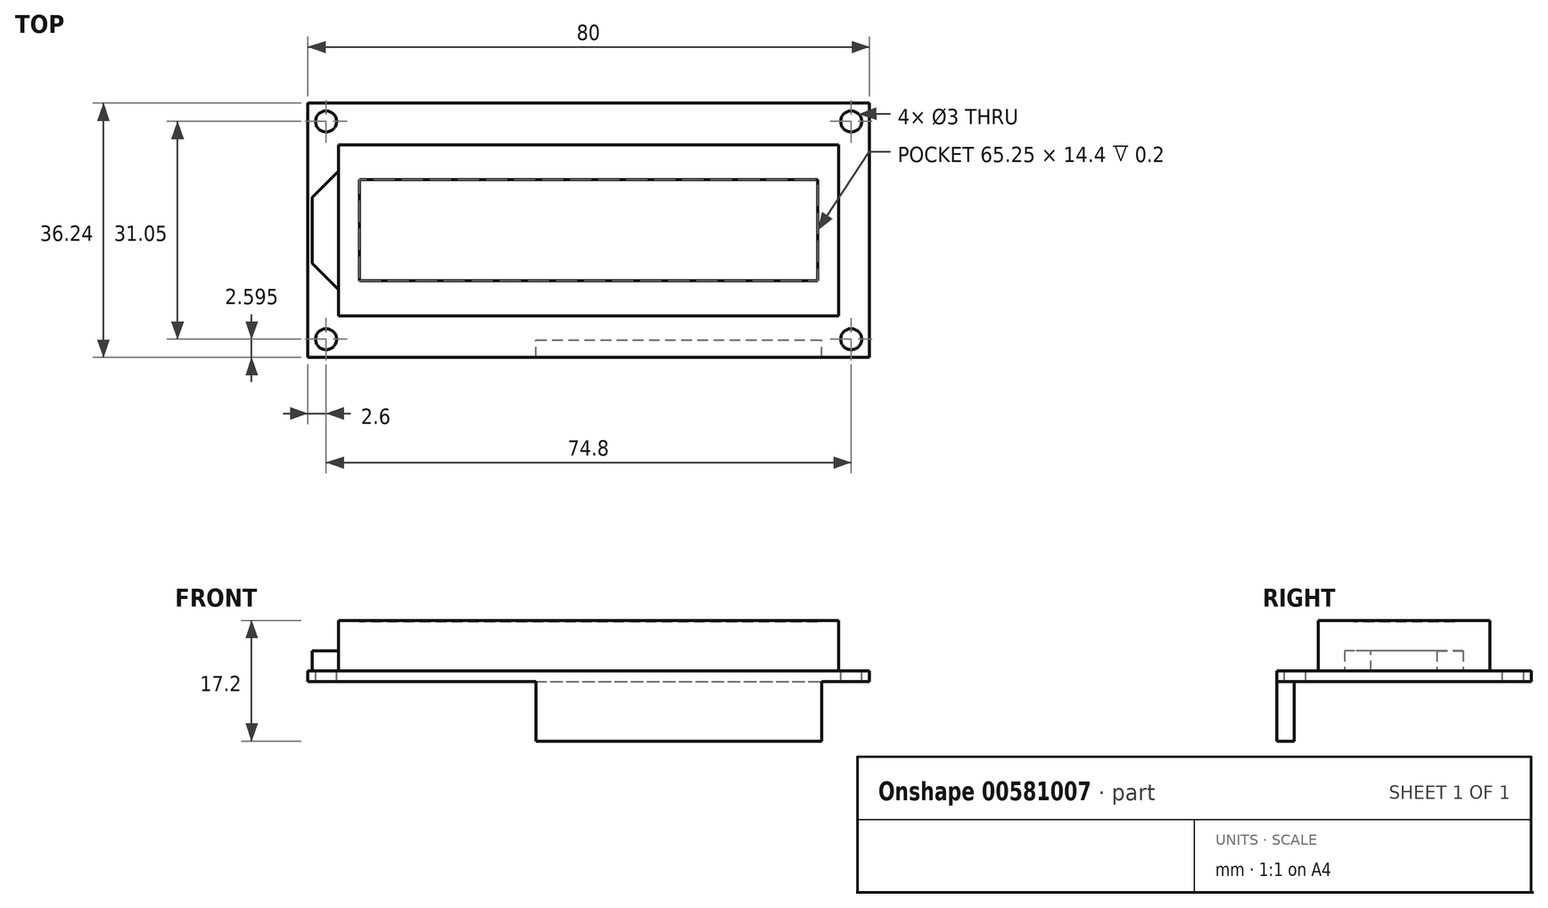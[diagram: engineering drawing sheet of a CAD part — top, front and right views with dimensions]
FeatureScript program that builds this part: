
annotation { "Feature Type Name" : "Feature", "Feature Type Description" : "" }
export const myFeature = defineFeature(function(context is Context, id is Id, definition is map)
    precondition{}
    {
        {
            var Q0;
            Q0=qCreatedBy(makeId("Top.planeOp"),FACE);
            var sketch = newSketch(context, id + "F0", { "sketchPlane" : qUnion([Q0])});
            skLineSegment(sketch, "E0.bottom", {"start": v(35.63, 12.2) * mm, "end": v(-35.63, 12.2) * mm});
            skLineSegment(sketch, "E0.top", {"start": v(35.63, -12.2) * mm, "end": v(-35.63, -12.2) * mm});
            skLineSegment(sketch, "E0.left", {"start": v(35.63, 12.2) * mm, "end": v(35.63, -12.2) * mm});
            skLineSegment(sketch, "E0.right", {"start": v(-35.63, 12.2) * mm, "end": v(-35.63, -12.2) * mm});
            skPoint(sketch, "E0.middle", {"position": v(0, 0) * mm});
            skLineSegment(sketch, "E1.bottom", {"start": v(-32.63, -7.2) * mm, "end": v(32.63, -7.2) * mm});
            skLineSegment(sketch, "E1.top", {"start": v(-32.63, 7.2) * mm, "end": v(32.63, 7.2) * mm});
            skLineSegment(sketch, "E1.left", {"start": v(-32.63, -7.2) * mm, "end": v(-32.63, 7.2) * mm});
            skLineSegment(sketch, "E1.right", {"start": v(32.63, -7.2) * mm, "end": v(32.63, 7.2) * mm});
            skSolve(sketch);
        }
        {
            var Q0;
            Q0=makeQuery(id+"F0.imprint","IMPRINT",FACE,{"disambiguationData":[TD([[makeQuery(id+"F0.imprint","IMPRINT",EDGE,{"derivedFrom":sQuery(id+"F0.wireOp",EDGE,"E0.bottom")}),1.0]])]});
            var Q1;
            Q1=makeQuery(id+"F0.imprint","IMPRINT",FACE,{"disambiguationData":[TD([[makeQuery(id+"F0.imprint","IMPRINT",EDGE,{"derivedFrom":sQuery(id+"F0.wireOp",EDGE,"E1.bottom")}),1.0]])]});
            extrude(context, id + "F1", {"entities" : qUnion([Q0, Q1]), "depth" : 7 * mm, "offsetDistance" : 25 * mm});
        }
        {
            var Q0;
            Q0 = qSketchRegion(id + "F0", true);
            extrude(context, id + "F2", {"entities" : qUnion([Q0]), "operationType" : NewBodyOperationType.ADD, "depth" : 7.2 * mm, "offsetDistance" : 25 * mm});
        }
        {
            var Q0;
            {var subQ0=sQuery(id+"F0.wireOp",EDGE,"E0.right");Q0=makeQuery(id+"F2.boolean.opBoolean","MERGE",FACE,{"derivedFrom":[makeQuery(id+"F1.opExtrude","SWEPT_FACE",FACE,{"disambiguationData":[OSD([subQ0])]}),makeQuery(id+"F2.opExtrude","SWEPT_FACE",FACE,{"disambiguationData":[OSD([subQ0])]})]});}
            var sketch = newSketch(context, id + "F3", { "sketchPlane" : qUnion([Q0])});
            skLineSegment(sketch, "E2.bottom", {"start": v(-8.7, 0) * mm, "end": v(8.7, 0) * mm});
            skLineSegment(sketch, "E2.top", {"start": v(-8.7, 2.85) * mm, "end": v(8.7, 2.85) * mm});
            skLineSegment(sketch, "E2.left", {"start": v(-8.7, 0) * mm, "end": v(-8.7, 2.85) * mm});
            skLineSegment(sketch, "E2.right", {"start": v(8.7, 0) * mm, "end": v(8.7, 2.85) * mm});
            skSolve(sketch);
        }
        {
            var Q0;
            Q0=makeQuery(id+"F3.imprint","IMPRINT",FACE,{"disambiguationData":[TD([[makeQuery(id+"F3.imprint","IMPRINT",EDGE,{"derivedFrom":sQuery(id+"F3.wireOp",EDGE,"E2.bottom")}),1.0]])]});
            extrude(context, id + "F4", {"entities" : qUnion([Q0]), "operationType" : NewBodyOperationType.ADD, "depth" : 3.75 * mm, "offsetDistance" : 25 * mm});
        }
        {
            var Q0;
            Q0=makeQuery(id+"F4.opExtrude","CAP_EDGE",EDGE,{"disambiguationData":[OSD([sQuery(id+"F3.wireOp",EDGE,"E2.right")])],"isStart":false});
            var Q1;
            Q1=makeQuery(id+"F4.opExtrude","CAP_EDGE",EDGE,{"disambiguationData":[OSD([sQuery(id+"F3.wireOp",EDGE,"E2.left")])],"isStart":false});
            chamfer(context, id + "F5", {"entities" : qUnion([Q0, Q1]), "width" : 4 * mm, "tangentPropagation" : true});
        }
        {
            var Q0;
            Q0=qCreatedBy(makeId("Top.planeOp"),FACE);
            var sketch = newSketch(context, id + "F6", { "sketchPlane" : qUnion([Q0])});
            skLineSegment(sketch, "E3.bottom", {"start": v(-40, -18.12) * mm, "end": v(40, -18.12) * mm});
            skLineSegment(sketch, "E3.top", {"start": v(-40, 18.12) * mm, "end": v(40, 18.12) * mm});
            skLineSegment(sketch, "E3.left", {"start": v(-40, -18.12) * mm, "end": v(-40, 18.12) * mm});
            skLineSegment(sketch, "E3.right", {"start": v(40, -18.12) * mm, "end": v(40, 18.12) * mm});
            skPoint(sketch, "E3.middle", {"position": v(0, 0) * mm});
            skCircle(sketch, "E4", {"center": v(37.4, 15.52) * mm, "radius": 1.5 * mm});
            skCircle(sketch, "E5", {"center": v(-37.4, 15.52) * mm, "radius": 1.5 * mm});
            skCircle(sketch, "E6", {"center": v(-37.4, -15.52) * mm, "radius": 1.5 * mm});
            skCircle(sketch, "E7", {"center": v(37.4, -15.52) * mm, "radius": 1.5 * mm});
            skSolve(sketch);
        }
        {
            var Q0;
            Q0=makeQuery(id+"F6.imprint","IMPRINT",FACE,{"disambiguationData":[TD([[makeQuery(id+"F6.imprint","IMPRINT",EDGE,{"derivedFrom":sQuery(id+"F6.wireOp",EDGE,"E3.bottom")}),1.0]])]});
            extrude(context, id + "F7", {"entities" : qUnion([Q0]), "operationType" : NewBodyOperationType.ADD, "oppositeDirection" : true, "depth" : 1.5 * mm, "offsetDistance" : 25 * mm});
        }
        {
            var Q0;
            Q0=makeQuery(id+"F7.opExtrude","CAP_FACE",FACE,{"disambiguationData":[OSD([sQuery(id+"F6.wireOp",EDGE,"E3.bottom"),sQuery(id+"F6.wireOp",EDGE,"E3.top"),sQuery(id+"F6.wireOp",EDGE,"E3.left"),sQuery(id+"F6.wireOp",EDGE,"E3.right"),sQuery(id+"F6.wireOp",EDGE,"E4"),sQuery(id+"F6.wireOp",EDGE,"E5"),sQuery(id+"F6.wireOp",EDGE,"E6"),sQuery(id+"F6.wireOp",EDGE,"E7")])],"isStart":false});
            var sketch = newSketch(context, id + "F8", { "sketchPlane" : qUnion([Q0])});
            skLineSegment(sketch, "E8.bottom", {"start": v(-7.5, 18.12) * mm, "end": v(33.2, 18.12) * mm});
            skLineSegment(sketch, "E8.top", {"start": v(-7.5, 15.62) * mm, "end": v(33.2, 15.62) * mm});
            skLineSegment(sketch, "E8.left", {"start": v(-7.5, 18.12) * mm, "end": v(-7.5, 15.62) * mm});
            skLineSegment(sketch, "E8.right", {"start": v(33.2, 18.12) * mm, "end": v(33.2, 15.62) * mm});
            skSolve(sketch);
        }
        {
            var Q0;
            Q0=makeQuery(id+"F8.imprint","IMPRINT",FACE,{"disambiguationData":[TD([[makeQuery(id+"F8.imprint","IMPRINT",EDGE,{"derivedFrom":sQuery(id+"F8.wireOp",EDGE,"E8.bottom")}),-1.0]])]});
            extrude(context, id + "F9", {"entities" : qUnion([Q0]), "operationType" : NewBodyOperationType.ADD, "depth" : 8.5 * mm, "offsetDistance" : 25 * mm});
        }
    });
